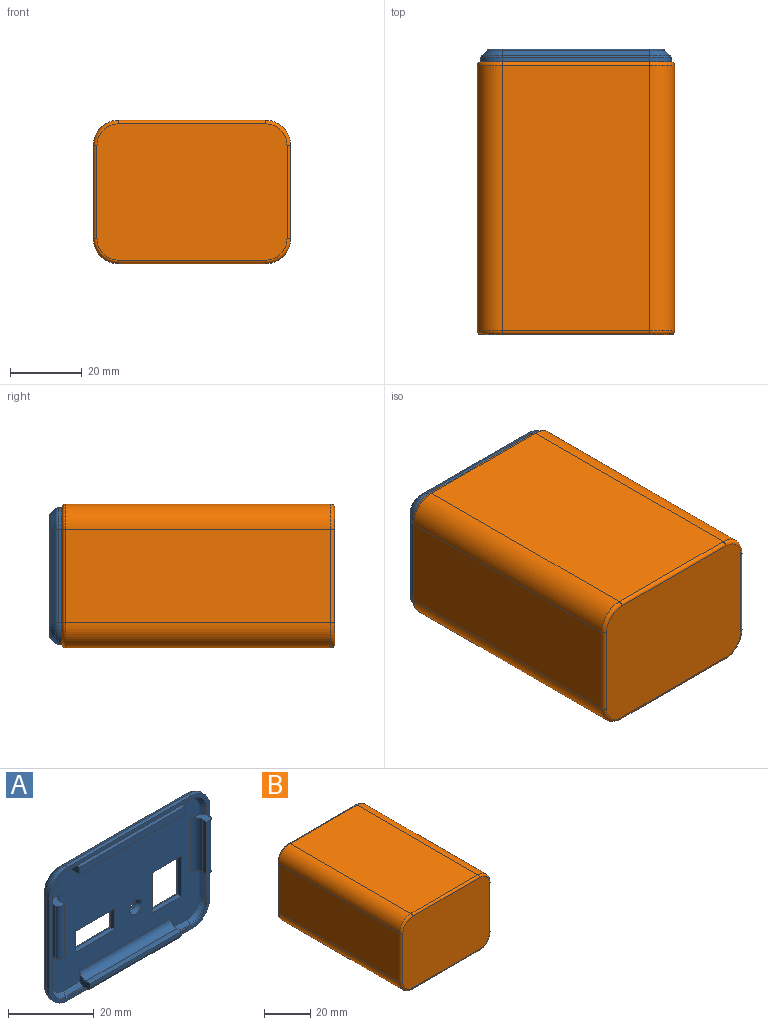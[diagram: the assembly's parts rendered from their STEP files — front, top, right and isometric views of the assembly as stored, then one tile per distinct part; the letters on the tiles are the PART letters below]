
ASSEMBLY  parts=2 mates=1
PART A: 104 faces, bbox 54x5.5x39 mm
  f0: plane 49x34mm, normal (0,-1,0), area 1237.4mm2, adj f24,f25,f26,f28,f30,f34,f36,f39
  f1: plane 48.17x33.17mm, normal (0,1,0), area 1328.1mm2, adj f53,f54,f55,f56,f57,f58,f59,f60
  f2: plane 9x0.5mm, normal (-1,0,0), area 4.5mm2, adj f11,f22,f40,f92
  f3: plane 9x0.5mm, normal (1,0,0), area 4.5mm2, adj f10,f22,f36,f89
  f4: plane 5.55x0.5mm, normal (0,0,1), area 2.8mm2, adj f10,f22,f28,f91
  f5: plane 2x0.5mm, normal (1,0,0), area 1mm2, adj f13,f22,f34,f95
  f6: plane 5.45x0.5mm, normal (0,0,1), area 2.7mm2, adj f11,f22,f30,f94
  f7: plane 2x0.5mm, normal (-1,0,0), area 1mm2, adj f12,f22,f39,f100
  f8: plane 3x0.5mm, normal (0,0,-1), area 1.5mm2, adj f13,f22,f26,f97
  f9: plane 3x0.5mm, normal (0,0,-1), area 1.5mm2, adj f12,f22,f24,f98
  f10: cylinder r=5mm len=5mm, axis (0,-1,0), area 3.9mm2, adj f3,f4,f22,f90
  f11: cylinder r=5mm len=5mm, axis (0,-1,0), area 3.9mm2, adj f2,f6,f22,f93
  f12: cylinder r=5mm len=5mm, axis (0,-1,0), area 3.9mm2, adj f7,f9,f22,f99
  f13: cylinder r=5mm len=5mm, axis (0,-1,0), area 3.9mm2, adj f5,f8,f22,f96
  f14: cylinder r=6mm len=6mm, axis (0,-1,0), area 10.2mm2, adj f15,f21,f22,f76
  f15: plane 41x1.09mm, normal (0,0,-1), area 44.5mm2, adj f14,f16,f22,f77
  f16: cylinder r=6mm len=6mm, axis (0,-1,0), area 10.2mm2, adj f15,f17,f22,f75
  f17: plane 26x1.09mm, normal (-1,0,0), area 28.2mm2, adj f16,f18,f22,f73
  f18: cylinder r=6mm len=6mm, axis (0,-1,0), area 10.2mm2, adj f17,f19,f22,f71
  f19: plane 41x1.09mm, normal (0,0,1), area 44.5mm2, adj f18,f20,f22,f70
  f20: cylinder r=6mm len=6mm, axis (0,-1,0), area 10.2mm2, adj f19,f21,f22,f72
  f21: plane 26x1.09mm, normal (1,0,0), area 28.2mm2, adj f14,f20,f22,f74
  f22: plane 53x38mm, normal (0,-1,0), area 168.6mm2, adj f2,f3,f4,f5,f6,f7,f8,f9
  f23: plane 35x1mm, normal (0,0,1), area 35mm2, adj f22,f24,f26,f27
  f24: plane 2.5x2mm, normal (1,0,0), area 4.5mm2, adj f0,f9,f23,f25,f27,f98
  f25: plane 35x2.5mm, normal (0,0,-1), area 87.5mm2, adj f0,f24,f26,f27
  f26: plane 2.5x2mm, normal (-1,0,0), area 4.5mm2, adj f0,f8,f23,f25,f27,f97
  f27: plane 35x2mm, normal (0,-1,0), area 70mm2, adj f23,f24,f25,f26
  f28: plane 4x3.5mm, normal (-1,0,0), area 7.1mm2, adj f0,f4,f29,f31,f32,f88,f91,f102
  f29: plane 30x1.5mm, normal (0,0,1), area 45mm2, adj f28,f30,f32,f88
  f30: plane 4x3.5mm, normal (1,0,0), area 7.1mm2, adj f0,f6,f29,f31,f32,f88,f94,f102
  f31: plane 30x1mm, normal (0,0,-1), area 30mm2, adj f22,f28,f30,f102
  f32: plane 30x1mm, normal (0,-1,0), area 30mm2, adj f28,f29,f30,f102
  f33: plane 15x1mm, normal (-1,0,0), area 15mm2, adj f22,f34,f36,f101
  f34: plane 4x3.5mm, normal (0,0,1), area 7.1mm2, adj f0,f5,f33,f35,f37,f87,f95,f101
  f35: plane 15x1.5mm, normal (1,0,0), area 22.5mm2, adj f34,f36,f37,f87
  f36: plane 4x3.5mm, normal (0,0,-1), area 7.1mm2, adj f0,f3,f33,f35,f37,f87,f89,f101
  f37: plane 15x1mm, normal (0,-1,0), area 15mm2, adj f34,f35,f36,f101
  f38: plane 15x1mm, normal (1,0,0), area 15mm2, adj f22,f39,f40,f103
  f39: plane 4x3.5mm, normal (0,0,1), area 7.1mm2, adj f0,f7,f38,f41,f42,f86,f100,f103
  f40: plane 4x3.5mm, normal (0,0,-1), area 7.1mm2, adj f0,f2,f38,f41,f42,f86,f92,f103
  f41: plane 15x1.5mm, normal (-1,0,0), area 22.5mm2, adj f39,f40,f42,f86
  f42: plane 15x1mm, normal (0,-1,0), area 15mm2, adj f39,f40,f41,f103
  f43: plane 13x1.25mm, normal (0,0,-1), area 16.3mm2, adj f0,f44,f46,f55
  f44: plane 6x1.25mm, normal (-1,0,0), area 7.5mm2, adj f0,f43,f45,f57
  f45: plane 13x1.25mm, normal (0,0,1), area 16.3mm2, adj f0,f44,f46,f56
  f46: plane 6x1.25mm, normal (1,0,0), area 7.5mm2, adj f0,f43,f45,f54
  f47: cylinder r=1mm len=2mm, axis (0,1,0), area 3.1mm2, adj f52,f53
  f48: plane 9.5x1.25mm, normal (0,0,-1), area 11.9mm2, adj f0,f49,f51,f59
  f49: plane 11.5x1.25mm, normal (-1,0,0), area 14.4mm2, adj f0,f48,f50,f61
  f50: plane 9.5x1.25mm, normal (0,0,1), area 11.9mm2, adj f0,f49,f51,f60
  f51: plane 11.5x1.25mm, normal (1,0,0), area 14.4mm2, adj f0,f48,f50,f58
  f52: cone r=2mm half-angle=45deg, axis (0,-1,0), area 13.3mm2, adj f0,f47
  f53: torus R=1.5mm, axis (0,-1,0), area 5.8mm2, adj f1,f47
  f54: cylinder r=0.75mm len=7.5mm, axis (0,0,1), area 7.7mm2, adj f1,f46,f55,f56
  f55: cylinder r=0.75mm len=14.5mm, axis (1,0,0), area 16mm2, adj f1,f43,f54,f57
  f56: cylinder r=0.75mm len=14.5mm, axis (-1,0,0), area 16mm2, adj f1,f45,f54,f57
  f57: cylinder r=0.75mm len=7.5mm, axis (0,0,-1), area 7.7mm2, adj f1,f44,f55,f56
  f58: cylinder r=0.75mm len=13mm, axis (0,0,1), area 14.2mm2, adj f1,f51,f59,f60
  f59: cylinder r=0.75mm len=11mm, axis (1,0,0), area 11.8mm2, adj f1,f48,f58,f61
  f60: cylinder r=0.75mm len=11mm, axis (-1,0,0), area 11.8mm2, adj f1,f50,f58,f61
  f61: cylinder r=0.75mm len=13mm, axis (0,0,-1), area 14.2mm2, adj f1,f49,f59,f60
  f62: plane 41x1.41mm, normal (0,0.71,0.71), area 82mm2, adj f63,f64,f70,f78
  f63: cone r=4mm half-angle=45deg, axis (0,-1,0), area 15.7mm2, adj f62,f65,f72,f79
  f64: cone r=4mm half-angle=45deg, axis (0,-1,0), area 15.7mm2, adj f62,f66,f71,f80
  f65: plane 26x1.41mm, normal (0.71,0.71,0), area 52mm2, adj f63,f67,f74,f81
  f66: plane 26x1.41mm, normal (-0.71,0.71,0), area 52mm2, adj f64,f68,f73,f82
  f67: cone r=4mm half-angle=45deg, axis (0,-1,0), area 15.7mm2, adj f65,f69,f76,f83
  f68: cone r=4mm half-angle=45deg, axis (0,-1,0), area 15.7mm2, adj f66,f69,f75,f84
  f69: plane 41x1.41mm, normal (0,0.71,-0.71), area 82mm2, adj f67,f68,f77,f85
  f70: cylinder r=1mm len=41mm, axis (-1,0,0), area 32.2mm2, adj f19,f62,f71,f72
  f71: torus R=5mm, axis (0,1,0), area 7.3mm2, adj f18,f64,f70,f73
  f72: torus R=5mm, axis (0,1,0), area 7.3mm2, adj f20,f63,f70,f74
  f73: cylinder r=1mm len=26mm, axis (0,0,-1), area 20.4mm2, adj f17,f66,f71,f75
  f74: cylinder r=1mm len=26mm, axis (0,0,1), area 20.4mm2, adj f21,f65,f72,f76
  f75: torus R=5mm, axis (0,1,0), area 7.3mm2, adj f16,f68,f73,f77
  f76: torus R=5mm, axis (0,1,0), area 7.3mm2, adj f14,f67,f74,f77
  f77: cylinder r=1mm len=41mm, axis (1,0,0), area 32.2mm2, adj f15,f69,f75,f76
  f78: cylinder r=1mm len=41mm, axis (1,0,0), area 32.2mm2, adj f1,f62,f79,f80
  f79: torus R=3.59mm, axis (0,-1,0), area 4.9mm2, adj f1,f63,f78,f81
  f80: torus R=3.59mm, axis (0,-1,0), area 4.9mm2, adj f1,f64,f78,f82
  f81: cylinder r=1mm len=26mm, axis (0,0,-1), area 20.4mm2, adj f1,f65,f79,f83
  f82: cylinder r=1mm len=26mm, axis (0,0,1), area 20.4mm2, adj f1,f66,f80,f84
  f83: torus R=3.59mm, axis (0,-1,0), area 4.9mm2, adj f1,f67,f81,f85
  f84: torus R=3.59mm, axis (0,-1,0), area 4.9mm2, adj f1,f68,f82,f85
  f85: cylinder r=1mm len=41mm, axis (-1,0,0), area 32.2mm2, adj f1,f69,f83,f84
  f86: cylinder r=2mm len=15mm, axis (0,0,1), area 47.1mm2, adj f0,f39,f40,f41
  f87: cylinder r=2mm len=15mm, axis (0,0,-1), area 47.1mm2, adj f0,f34,f35,f36
  f88: cylinder r=2mm len=30mm, axis (1,0,0), area 94.2mm2, adj f0,f28,f29,f30
  f89: plane 9x1mm, normal (0.71,-0.71,0), area 12.7mm2, adj f0,f3,f36,f90
  f90: cone r=4mm half-angle=45deg, axis (0,-1,0), area 10mm2, adj f0,f10,f89,f91
  f91: plane 5.55x1mm, normal (0,-0.71,0.71), area 7.8mm2, adj f0,f4,f28,f90
  f92: plane 9x1mm, normal (-0.71,-0.71,0), area 12.7mm2, adj f0,f2,f40,f93
  f93: cone r=4mm half-angle=45deg, axis (0,-1,0), area 10mm2, adj f0,f11,f92,f94
  f94: plane 5.45x1mm, normal (0,-0.71,0.71), area 7.7mm2, adj f0,f6,f30,f93
  f95: plane 2x1mm, normal (0.71,-0.71,0), area 2.8mm2, adj f0,f5,f34,f96
  f96: cone r=4mm half-angle=45deg, axis (0,-1,0), area 10mm2, adj f0,f13,f95,f97
  f97: plane 3x1mm, normal (0,-0.71,-0.71), area 4.2mm2, adj f0,f8,f26,f96
  f98: plane 3x1mm, normal (0,-0.71,-0.71), area 4.2mm2, adj f0,f9,f24,f99
  f99: cone r=4mm half-angle=45deg, axis (0,-1,0), area 10mm2, adj f0,f12,f98,f100
  f100: plane 2x1mm, normal (-0.71,-0.71,0), area 2.8mm2, adj f0,f7,f39,f99
  f101: cylinder r=1mm len=15mm, axis (0,0,-1), area 23.6mm2, adj f33,f34,f36,f37
  f102: cylinder r=1mm len=30mm, axis (1,0,0), area 47.1mm2, adj f28,f30,f31,f32
  f103: cylinder r=1mm len=15mm, axis (0,0,1), area 23.6mm2, adj f38,f39,f40,f42
PART B: 52 faces, bbox 56.2x76x41.2 mm
  f0: plane 74.5x26mm, normal (1,0,0), area 1791mm2, adj f2,f4,f9,f14,f19,f33
  f1: plane 74.5x26mm, normal (-1,0,0), area 1791mm2, adj f4,f5,f11,f14,f20,f32
  f2: plane 7x6.5mm, normal (0,1,0), area 10.5mm2, adj f0,f6,f8,f9,f18,f33
  f3: plane 74.5x41mm, normal (0,0,-1), area 2669.5mm2, adj f4,f14,f19,f20,f23,f24,f25,f27
  f4: plane 51x36mm, normal (0,1,0), area 1723.5mm2, adj f0,f1,f3,f6,f8,f9,f10,f11
  f5: plane 7x6.5mm, normal (0,1,0), area 10.5mm2, adj f1,f6,f10,f11,f17,f32
  f6: plane 74.5x41mm, normal (0,0,1), area 2835.5mm2, adj f2,f4,f5,f14,f17,f18,f32,f33
  f7: plane 74x41mm, normal (0,0,-1), area 3034mm2, adj f34,f35,f43,f51
  f8: plane 73x2mm, normal (1,0,0), area 146mm2, adj f2,f4,f9,f18
  f9: plane 73x1.5mm, normal (0,0,1), area 109.5mm2, adj f0,f2,f4,f8
  f10: plane 73x2mm, normal (-1,0,0), area 146mm2, adj f4,f5,f11,f17
  f11: plane 73x1.5mm, normal (0,0,1), area 109.5mm2, adj f1,f4,f5,f10
  f12: plane 53x38mm, normal (0,-1,0), area 1983.1mm2, adj f44,f45,f46,f47,f48,f49,f50,f51
  f13: plane 74x26mm, normal (1,0,0), area 1924mm2, adj f22,f35,f39,f47
  f14: plane 53x38mm, normal (0,1,0), area 168.6mm2, adj f0,f1,f3,f6,f19,f20,f32,f33
  f15: plane 74x26mm, normal (-1,0,0), area 1924mm2, adj f21,f34,f40,f48
  f16: plane 74x41mm, normal (0,0,1), area 3034mm2, adj f21,f22,f36,f44
  f17: cylinder r=5mm len=73mm, axis (0,1,0), area 573.3mm2, adj f4,f5,f6,f10
  f18: cylinder r=5mm len=73mm, axis (0,1,0), area 573.3mm2, adj f2,f4,f6,f8
  f19: cylinder r=5mm len=74.5mm, axis (0,-1,0), area 585.1mm2, adj f0,f3,f4,f14
  f20: cylinder r=5mm len=74.5mm, axis (0,1,0), area 585.1mm2, adj f1,f3,f4,f14
  f21: cylinder r=7mm len=74mm, axis (0,1,0), area 813.7mm2, adj f15,f16,f38,f46
  f22: cylinder r=7mm len=74mm, axis (0,-1,0), area 813.7mm2, adj f13,f16,f37,f45
  f23: plane 35x2mm, normal (0,1,0), area 70mm2, adj f3,f24,f25,f26
  f24: plane 5.5x2mm, normal (-1,0,0), area 5.4mm2, adj f3,f23,f26,f31
  f25: plane 5.5x2mm, normal (1,0,0), area 5.4mm2, adj f3,f23,f26,f31
  f26: plane 35x1.5mm, normal (0,0,-1), area 52.5mm2, adj f23,f24,f25,f31
  f27: plane 5.5x2mm, normal (-1,0,0), area 5.4mm2, adj f3,f4,f29,f30
  f28: plane 5.5x2mm, normal (1,0,0), area 5.4mm2, adj f3,f4,f29,f30
  f29: plane 35x1.5mm, normal (0,0,-1), area 52.5mm2, adj f4,f27,f28,f30
  f30: cylinder r=5mm len=35mm, axis (1,0,0), area 162.3mm2, adj f3,f27,f28,f29
  f31: cylinder r=5mm len=35mm, axis (1,0,0), area 162.3mm2, adj f3,f24,f25,f26
  f32: cylinder r=5mm len=5mm, axis (0,1,0), area 11.8mm2, adj f1,f5,f6,f14
  f33: cylinder r=5mm len=5mm, axis (0,-1,0), area 11.8mm2, adj f0,f2,f6,f14
  f34: cylinder r=7mm len=74mm, axis (0,-1,0), area 813.7mm2, adj f7,f15,f42,f50
  f35: cylinder r=7mm len=74mm, axis (0,1,0), area 813.7mm2, adj f7,f13,f41,f49
  f36: cylinder r=1mm len=41mm, axis (1,0,0), area 64.4mm2, adj f14,f16,f37,f38
  f37: torus R=6mm, axis (0,-1,0), area 16.4mm2, adj f14,f22,f36,f39
  f38: torus R=6mm, axis (0,-1,0), area 16.4mm2, adj f14,f21,f36,f40
  f39: cylinder r=1mm len=26mm, axis (0,0,1), area 40.8mm2, adj f13,f14,f37,f41
  f40: cylinder r=1mm len=26mm, axis (0,0,-1), area 40.8mm2, adj f14,f15,f38,f42
  f41: torus R=6mm, axis (0,-1,0), area 16.4mm2, adj f14,f35,f39,f43
  f42: torus R=6mm, axis (0,-1,0), area 16.4mm2, adj f14,f34,f40,f43
  f43: cylinder r=1mm len=41mm, axis (-1,0,0), area 64.4mm2, adj f7,f14,f41,f42
  f44: cylinder r=1mm len=41mm, axis (-1,0,0), area 64.4mm2, adj f12,f16,f45,f46
  f45: torus R=6mm, axis (0,-1,0), area 16.4mm2, adj f12,f22,f44,f47
  f46: torus R=6mm, axis (0,-1,0), area 16.4mm2, adj f12,f21,f44,f48
  f47: cylinder r=1mm len=26mm, axis (0,0,-1), area 40.8mm2, adj f12,f13,f45,f49
  f48: cylinder r=1mm len=26mm, axis (0,0,1), area 40.8mm2, adj f12,f15,f46,f50
  f49: torus R=6mm, axis (0,-1,0), area 16.4mm2, adj f12,f35,f47,f51
  f50: torus R=6mm, axis (0,-1,0), area 16.4mm2, adj f12,f34,f48,f51
  f51: cylinder r=1mm len=41mm, axis (1,0,0), area 64.4mm2, adj f7,f12,f49,f50
PLACE A t=(0.03,20.29,0.48)mm
PLACE B t=(-0.01,20.27,-19.51)mm
MATE parallel B.f14 <-> A.f22  axis (0,1,0) through (-0.01,58.27,19.49)mm
